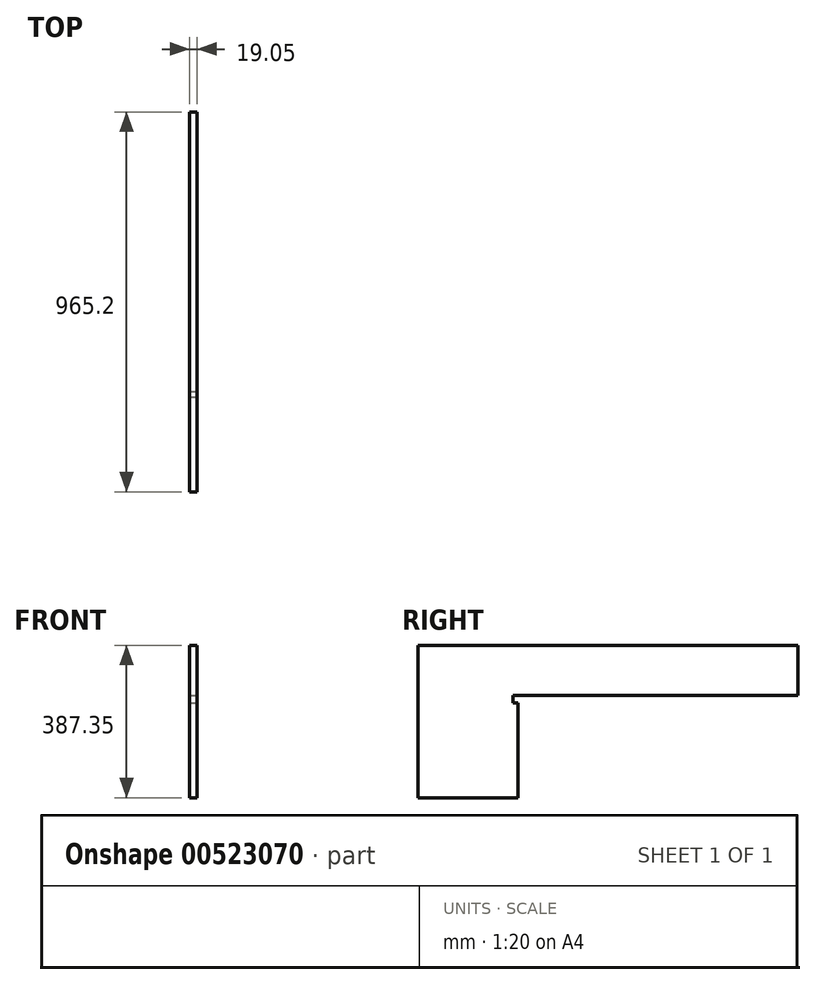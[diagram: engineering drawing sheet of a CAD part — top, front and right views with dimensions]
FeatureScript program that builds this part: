
annotation { "Feature Type Name" : "Feature", "Feature Type Description" : "" }
export const myFeature = defineFeature(function(context is Context, id is Id, definition is map)
    precondition{}
    {
        {
            var Q0;
            Q0=qCreatedBy(makeId("Right.planeOp"),FACE);
            var sketch = newSketch(context, id + "F0", { "sketchPlane" : qUnion([Q0])});
            skLineSegment(sketch, "E0.bottom", {"start": v(0, 0) * mm, "end": v(254, 0) * mm});
            skLineSegment(sketch, "E0.top", {"start": v(0, 387.35) * mm, "end": v(254, 387.35) * mm});
            skLineSegment(sketch, "E0.left", {"start": v(0, 0) * mm, "end": v(0, 387.35) * mm});
            skLineSegment(sketch, "E0.right", {"start": v(254, 0) * mm, "end": v(254, 387.35) * mm});
            skSolve(sketch);
        }
        {
            var Q0;
            Q0 = qSketchRegion(id + "F0", true);
            extrude(context, id + "F1", {"entities" : qUnion([Q0]), "depth" : 19.05 * mm, "offsetDistance" : 25.4 * mm});
        }
        {
            var Q0;
            Q0=makeQuery(id+"F1.opExtrude","CAP_FACE",FACE,{"disambiguationData":[OSD([sQuery(id+"F0.wireOp",EDGE,"E0.bottom"),sQuery(id+"F0.wireOp",EDGE,"E0.top"),sQuery(id+"F0.wireOp",EDGE,"E0.left"),sQuery(id+"F0.wireOp",EDGE,"E0.right")])],"isStart":false});
            var sketch = newSketch(context, id + "F2", { "sketchPlane" : qUnion([Q0])});
            skLineSegment(sketch, "E1.bottom", {"start": v(254, 387.35) * mm, "end": v(241.3, 387.35) * mm});
            skLineSegment(sketch, "E1.top", {"start": v(254, 241.3) * mm, "end": v(241.3, 241.3) * mm});
            skLineSegment(sketch, "E1.left", {"start": v(254, 387.35) * mm, "end": v(254, 241.3) * mm});
            skLineSegment(sketch, "E1.right", {"start": v(241.3, 387.35) * mm, "end": v(241.3, 241.3) * mm});
            skSolve(sketch);
        }
        {
            var Q0;
            Q0 = qSketchRegion(id + "F2", true);
            extrude(context, id + "F3", {"entities" : qUnion([Q0]), "operationType" : NewBodyOperationType.REMOVE, "endBound" : BoundingType.THROUGH_ALL, "oppositeDirection" : true, "depth" : 25.4 * mm, "offsetDistance" : 25.4 * mm});
        }
        {
            var Q0;
            Q0=makeQuery(id+"F1.opExtrude","CAP_FACE",FACE,{"disambiguationData":[OSD([sQuery(id+"F0.wireOp",EDGE,"E0.bottom"),sQuery(id+"F0.wireOp",EDGE,"E0.top"),sQuery(id+"F0.wireOp",EDGE,"E0.left"),sQuery(id+"F0.wireOp",EDGE,"E0.right")])],"isStart":false});
            var sketch = newSketch(context, id + "F4", { "sketchPlane" : qUnion([Q0])});
            skLineSegment(sketch, "E2.bottom", {"start": v(241.3, 387.35) * mm, "end": v(965.2, 387.35) * mm});
            skLineSegment(sketch, "E2.top", {"start": v(241.3, 260.35) * mm, "end": v(965.2, 260.35) * mm});
            skLineSegment(sketch, "E2.left", {"start": v(241.3, 387.35) * mm, "end": v(241.3, 260.35) * mm});
            skLineSegment(sketch, "E2.right", {"start": v(965.2, 387.35) * mm, "end": v(965.2, 260.35) * mm});
            skSolve(sketch);
        }
        {
            var Q0;
            Q0 = qSketchRegion(id + "F4", true);
            extrude(context, id + "F5", {"entities" : qUnion([Q0]), "operationType" : NewBodyOperationType.ADD, "oppositeDirection" : true, "depth" : 19.05 * mm, "offsetDistance" : 25.4 * mm});
        }
    });
